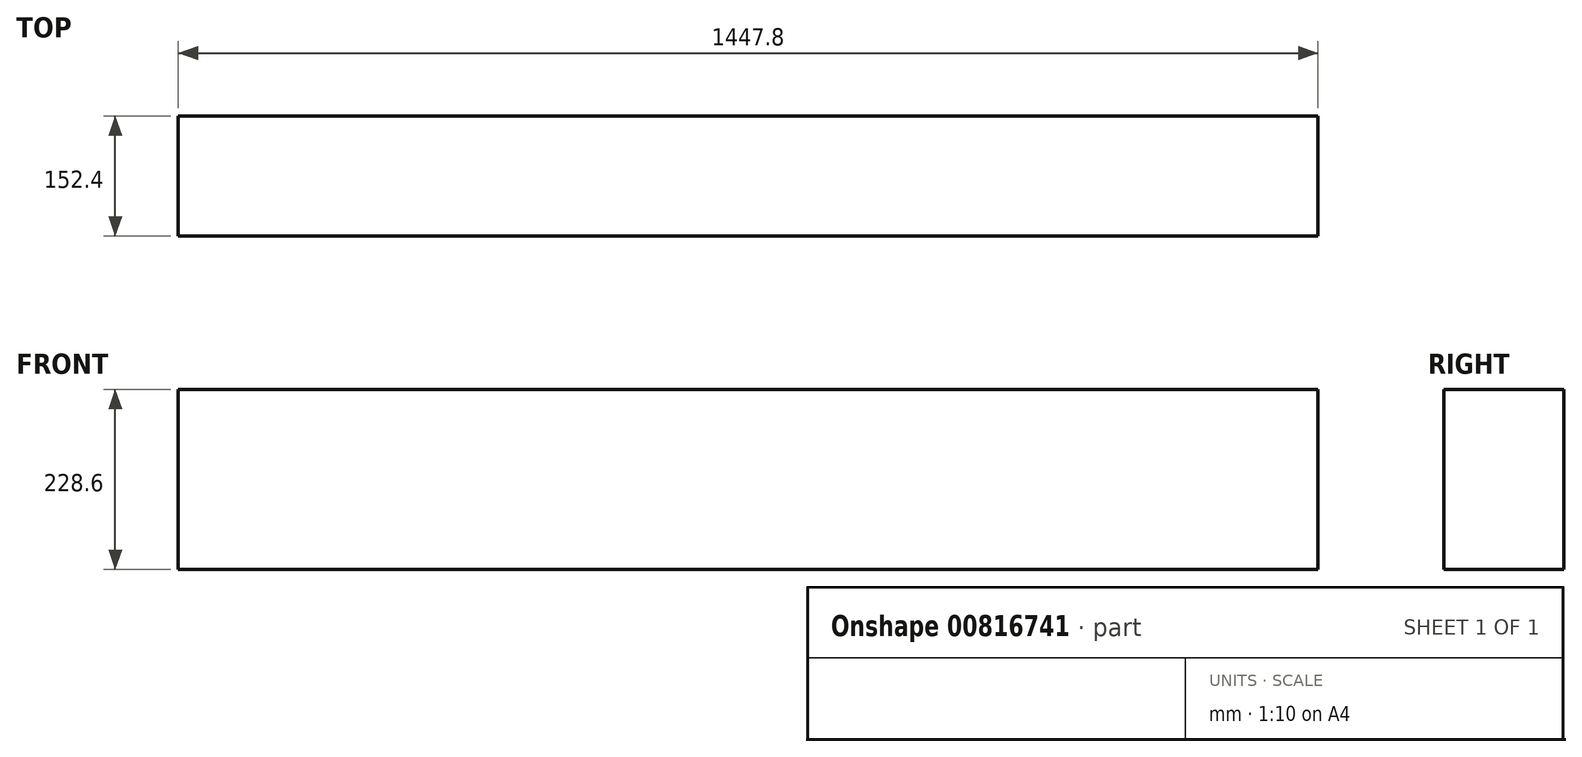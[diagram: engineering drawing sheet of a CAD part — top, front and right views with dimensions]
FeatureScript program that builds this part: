
annotation { "Feature Type Name" : "Feature", "Feature Type Description" : "" }
export const myFeature = defineFeature(function(context is Context, id is Id, definition is map)
    precondition{}
    {
        {
            var Q0;
            Q0=qCreatedBy(makeId("Top.planeOp"),FACE);
            var sketch = newSketch(context, id + "F0", { "sketchPlane" : qUnion([Q0])});
            skLineSegment(sketch, "E0.bottom", {"start": v(1396.33, -34.74) * mm, "end": v(-51.47, -34.74) * mm});
            skLineSegment(sketch, "E0.top", {"start": v(1396.33, 117.66) * mm, "end": v(-51.47, 117.66) * mm});
            skLineSegment(sketch, "E0.left", {"start": v(1396.33, -34.74) * mm, "end": v(1396.33, 117.66) * mm});
            skLineSegment(sketch, "E0.right", {"start": v(-51.47, -34.74) * mm, "end": v(-51.47, 117.66) * mm});
            skPoint(sketch, "E0.middle", {"position": v(672.43, 41.46) * mm});
            skSolve(sketch);
        }
        {
            var Q0;
            Q0 = qSketchRegion(id + "F0", true);
            extrude(context, id + "F1", {"entities" : qUnion([Q0]), "depth" : 228.6 * mm, "offsetDistance" : 25.4 * mm});
        }
    });
